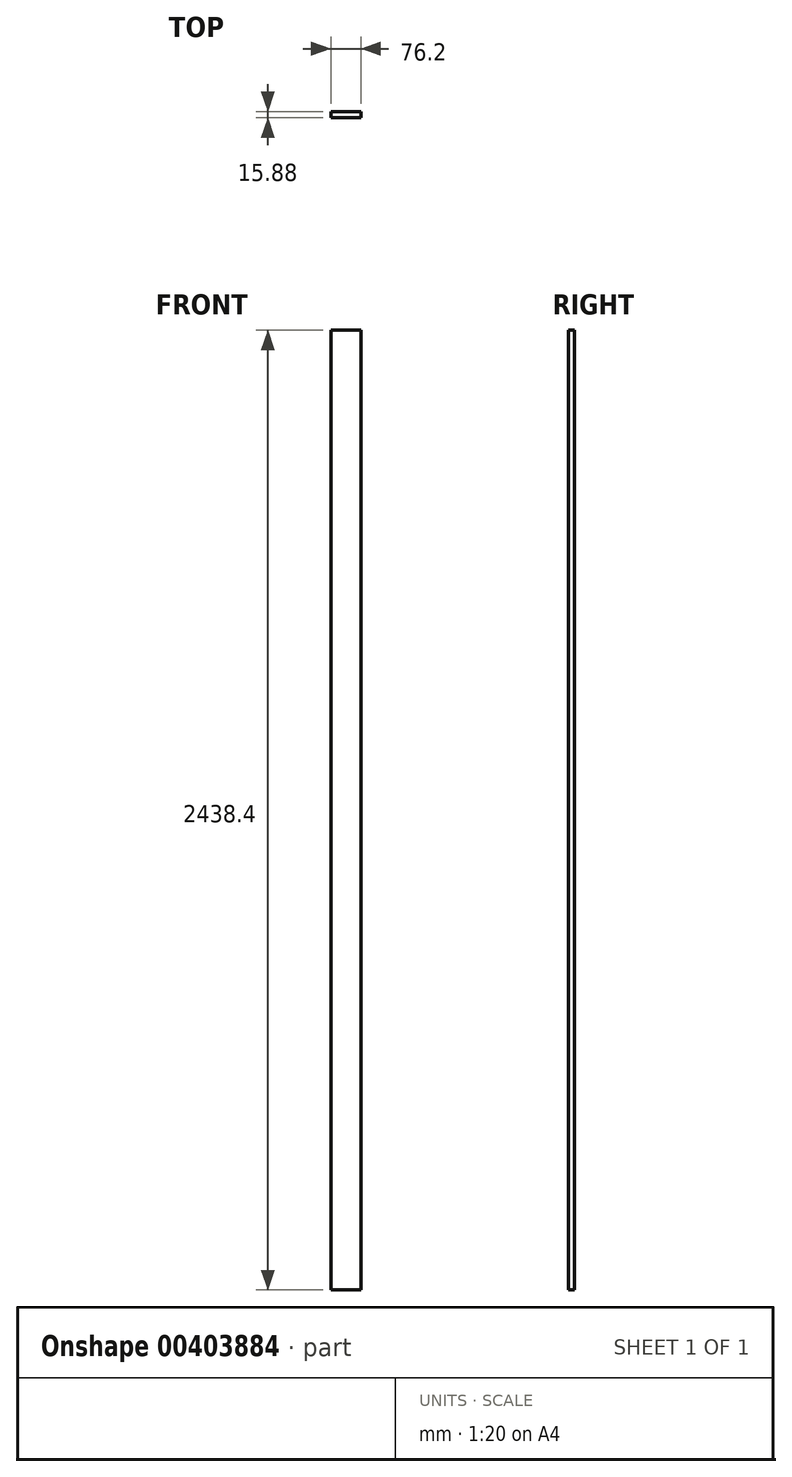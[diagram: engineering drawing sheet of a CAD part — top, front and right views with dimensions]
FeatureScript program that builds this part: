
annotation { "Feature Type Name" : "Feature", "Feature Type Description" : "" }
export const myFeature = defineFeature(function(context is Context, id is Id, definition is map)
    precondition{}
    {
        {
            var Q0;
            Q0=qCreatedBy(makeId("Front.planeOp"),FACE);
            var sketch = newSketch(context, id + "F0", { "sketchPlane" : qUnion([Q0])});
            skLineSegment(sketch, "E0.bottom", {"start": v(38.1, -1219.2) * mm, "end": v(-38.1, -1219.2) * mm});
            skLineSegment(sketch, "E0.top", {"start": v(38.1, 1219.2) * mm, "end": v(-38.1, 1219.2) * mm});
            skLineSegment(sketch, "E0.left", {"start": v(38.1, -1219.2) * mm, "end": v(38.1, 1219.2) * mm});
            skLineSegment(sketch, "E0.right", {"start": v(-38.1, -1219.2) * mm, "end": v(-38.1, 1219.2) * mm});
            skPoint(sketch, "E0.middle", {"position": v(0, 0) * mm});
            skSolve(sketch);
        }
        {
            var Q0;
            Q0 = qSketchRegion(id + "F0", true);
            extrude(context, id + "F1", {"entities" : qUnion([Q0]), "oppositeDirection" : true, "depth" : 15.88 * mm});
        }
    });
